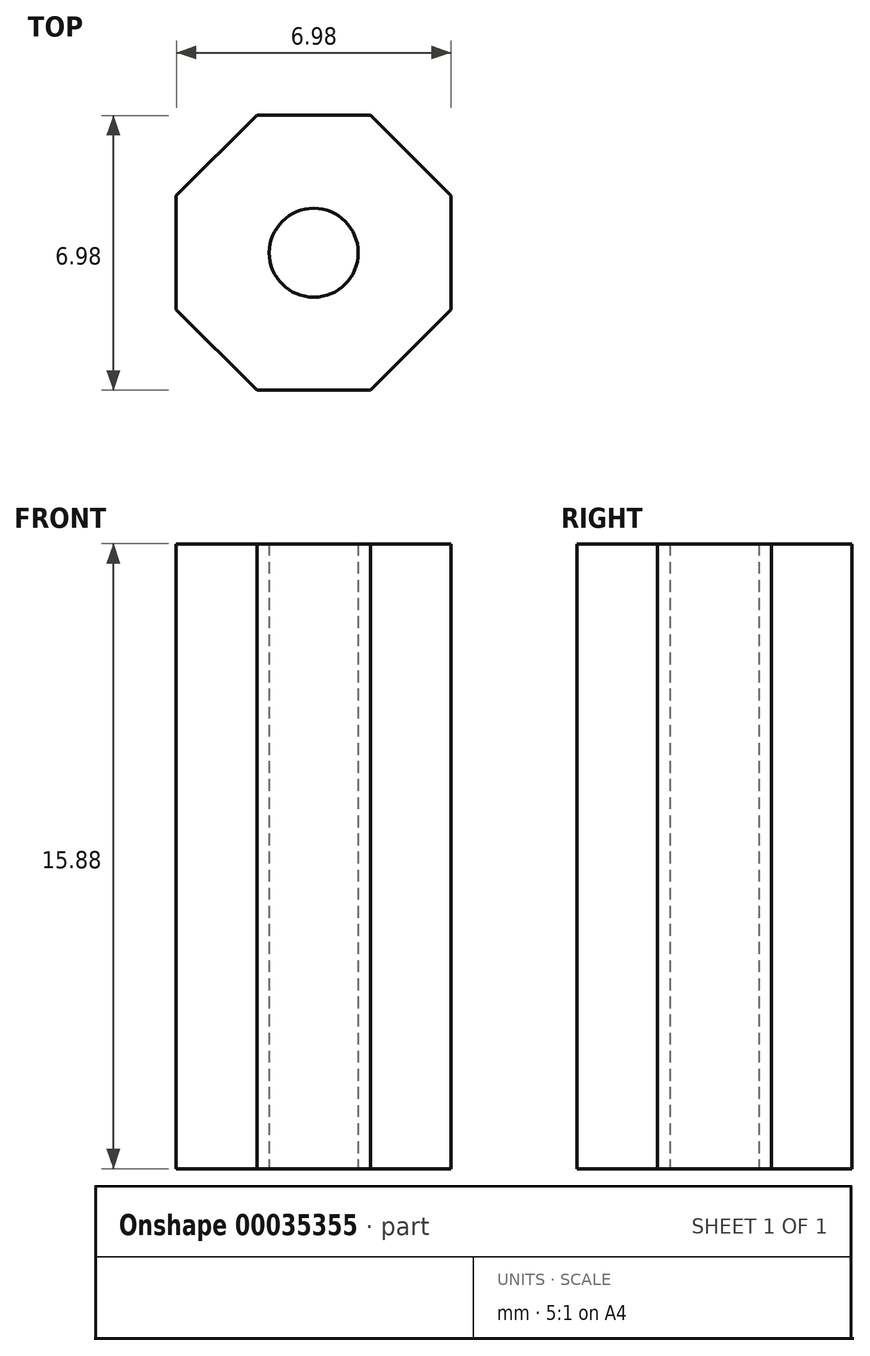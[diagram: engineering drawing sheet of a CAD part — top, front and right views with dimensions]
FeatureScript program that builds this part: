
annotation { "Feature Type Name" : "Feature", "Feature Type Description" : "" }
export const myFeature = defineFeature(function(context is Context, id is Id, definition is map)
    precondition{}
    {
        {
            var Q0;
            Q0=qCreatedBy(makeId("Top.planeOp"),FACE);
            var sketch = newSketch(context, id + "F0", { "sketchPlane" : qUnion([Q0])});
            skCircle(sketch, "E0.cCircle", {"center": v(0, 0) * mm, "radius": 3.5 * mm, "construction": true});
            skLineSegment(sketch, "E0.0", {"start": v(1.45, 3.5) * mm, "end": v(3.5, 1.45) * mm});
            skLineSegment(sketch, "E0.1", {"start": v(3.5, 1.45) * mm, "end": v(3.5, -1.45) * mm});
            skLineSegment(sketch, "E0.2", {"start": v(3.5, -1.45) * mm, "end": v(1.45, -3.5) * mm});
            skLineSegment(sketch, "E0.3", {"start": v(1.45, -3.5) * mm, "end": v(-1.45, -3.5) * mm});
            skLineSegment(sketch, "E0.4", {"start": v(-1.45, -3.5) * mm, "end": v(-3.5, -1.45) * mm});
            skLineSegment(sketch, "E0.5", {"start": v(-3.5, -1.45) * mm, "end": v(-3.5, 1.45) * mm});
            skLineSegment(sketch, "E0.6", {"start": v(-3.5, 1.45) * mm, "end": v(-1.45, 3.5) * mm});
            skLineSegment(sketch, "E0.7", {"start": v(-1.45, 3.5) * mm, "end": v(1.45, 3.5) * mm});
            skPoint(sketch, "E0.0.midPoint", {"position": v(2.47, 2.47) * mm});
            skSolve(sketch);
        }
        {
            var Q0;
            Q0 = qSketchRegion(id + "F0", true);
            extrude(context, id + "F1", {"entities" : qUnion([Q0]), "offsetDistance" : 25.4 * mm, "depth" : 15.88 * mm});
        }
        {
            var Q0;
            Q0=qCreatedBy(makeId("Top.planeOp"),FACE);
            var sketch = newSketch(context, id + "F2", { "sketchPlane" : qUnion([Q0])});
            skCircle(sketch, "E1", {"center": v(0, 0) * mm, "radius": 1.13 * mm});
            skSolve(sketch);
        }
        {
            var Q0;
            Q0=makeQuery(id+"F2.imprint","IMPRINT",FACE,{"disambiguationData":[TD([[makeQuery(id+"F2.imprint","IMPRINT",EDGE,{"derivedFrom":sQuery(id+"F2.wireOp",EDGE,"E1")}),1.0]])]});
            var Q1;
            Q1=sQuery(id+"F2.wireOp",EDGE,"E1");
            extrude(context, id + "F3", {"entities" : qUnion([Q0]), "operationType" : NewBodyOperationType.REMOVE, "surfaceEntities" : qUnion([Q1]), "endBound" : BoundingType.THROUGH_ALL, "offsetDistance" : 25.4 * mm, "depth" : 25.4 * mm});
        }
    });
